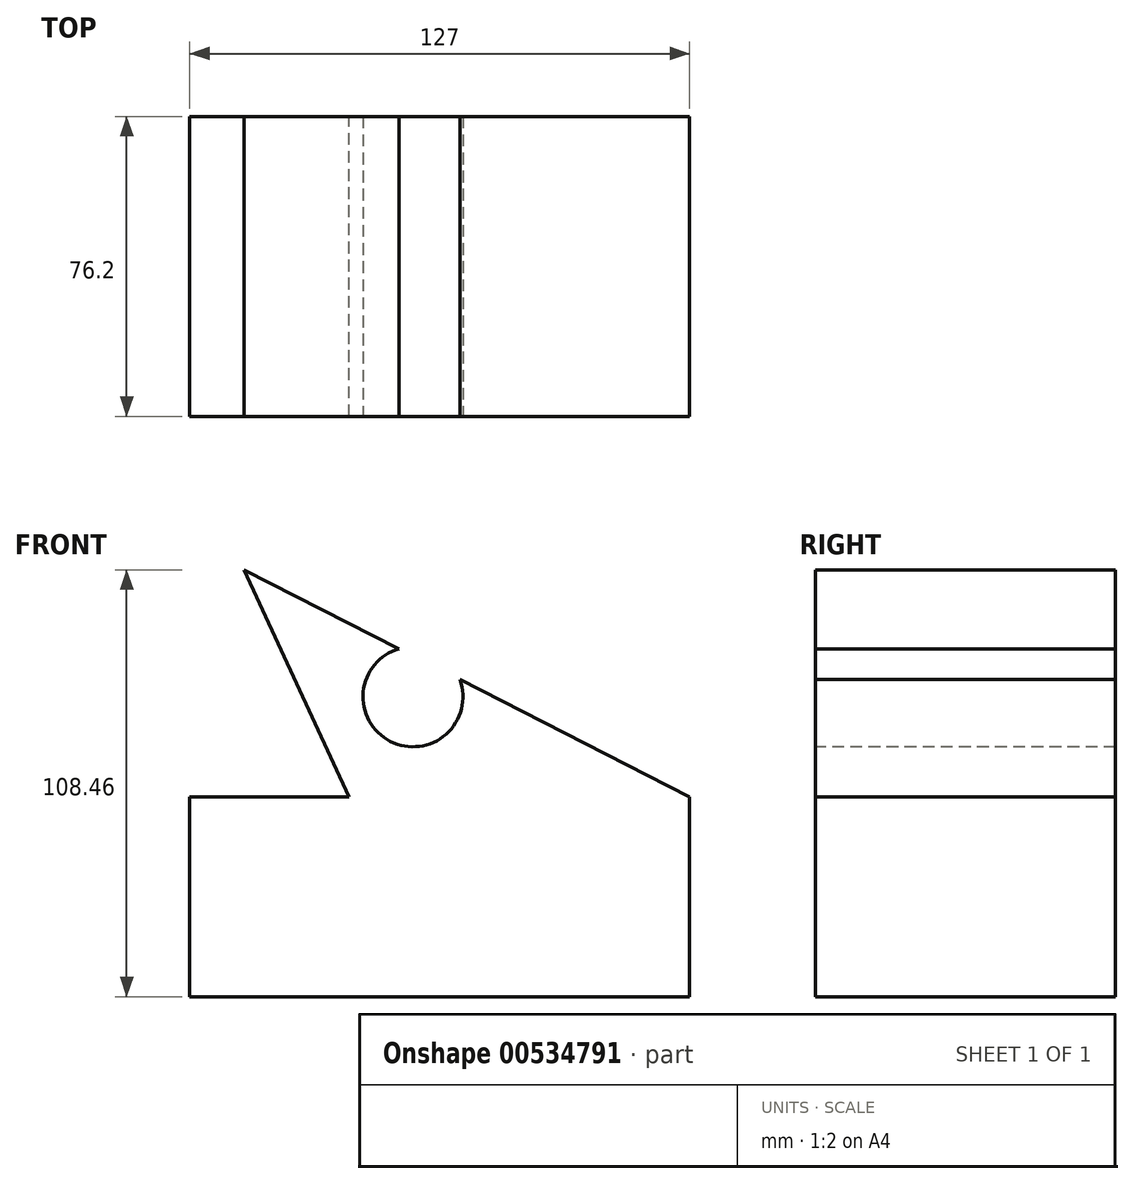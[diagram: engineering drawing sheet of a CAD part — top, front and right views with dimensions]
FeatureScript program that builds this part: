
annotation { "Feature Type Name" : "Feature", "Feature Type Description" : "" }
export const myFeature = defineFeature(function(context is Context, id is Id, definition is map)
    precondition{}
    {
        {
            var Q0;
            Q0=qCreatedBy(makeId("Front.planeOp"),FACE);
            var sketch = newSketch(context, id + "F0", { "sketchPlane" : qUnion([Q0])});
            skLineSegment(sketch, "E0.bottom", {"start": v(-93.7, 20.87) * mm, "end": v(-53.25, 20.87) * mm});
            skLineSegment(sketch, "E0.top", {"start": v(-93.7, -29.93) * mm, "end": v(33.3, -29.93) * mm});
            skLineSegment(sketch, "E0.left", {"start": v(-93.7, 20.87) * mm, "end": v(-93.7, -29.93) * mm});
            skLineSegment(sketch, "E0.right", {"start": v(33.3, 20.87) * mm, "end": v(33.3, -29.93) * mm});
            skLineSegment(sketch, "E1", {"start": v(33.3, 20.87) * mm, "end": v(-79.85, 78.53) * mm});
            skLineSegment(sketch, "E2", {"start": v(-79.85, 78.53) * mm, "end": v(-53.25, 20.87) * mm});
            skSolve(sketch);
        }
        {
            var Q0;
            Q0=makeQuery(id+"F0.imprint","IMPRINT",FACE,{"disambiguationData":[TD([[makeQuery(id+"F0.imprint","IMPRINT",EDGE,{"derivedFrom":sQuery(id+"F0.wireOp",EDGE,"E0.bottom")}),-1.0]])]});
            extrude(context, id + "F1", {"entities" : qUnion([Q0]), "depth" : 76.2 * mm, "offsetDistance" : 25.4 * mm});
        }
        {
            var Q0;
            Q0=makeQuery(id+"F1.opExtrude","CAP_FACE",FACE,{"disambiguationData":[OSD([sQuery(id+"F0.wireOp",EDGE,"E0.bottom"),sQuery(id+"F0.wireOp",EDGE,"E0.top"),sQuery(id+"F0.wireOp",EDGE,"E0.left"),sQuery(id+"F0.wireOp",EDGE,"E0.right"),sQuery(id+"F0.wireOp",EDGE,"E1"),sQuery(id+"F0.wireOp",EDGE,"E2")])],"isStart":false});
            var sketch = newSketch(context, id + "F2", { "sketchPlane" : qUnion([Q0])});
            skCircle(sketch, "E3", {"center": v(-37, 46.27) * mm, "radius": 12.7 * mm});
            skSolve(sketch);
        }
        {
            var Q0;
            {var subQ0=sQuery(id+"F2.wireOp",EDGE,"E3");var subQ1=makeQuery(id+"F1.opExtrude","CAP_EDGE",EDGE,{"disambiguationData":[OSD([sQuery(id+"F0.wireOp",EDGE,"E1")])],"isStart":false});var subQ2=makeQuery(id+"F2.imprint","INTERSECT",VERTEX,{"disambiguationData":[OD(0.0)],"derivedFrom":[subQ1,subQ0]});Q0=makeQuery(id+"F2.imprint","IMPRINT",FACE,{"disambiguationData":[TD([[makeQuery(id+"F2.imprint","IMPRINT",EDGE,{"disambiguationData":[TD([[subQ2,1.0]])],"derivedFrom":subQ0}),1.0]])]});}
            extrude(context, id + "F3", {"entities" : qUnion([Q0]), "operationType" : NewBodyOperationType.REMOVE, "endBound" : BoundingType.UP_TO_NEXT, "oppositeDirection" : true, "depth" : 25.4 * mm, "offsetDistance" : 25.4 * mm});
        }
    });
